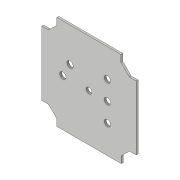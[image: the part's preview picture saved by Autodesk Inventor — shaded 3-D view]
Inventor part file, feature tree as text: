
AUTODESK INVENTOR PART (.ipt)
format: ipt  version: 2019.4 (Build 234330000, 330)  size: 149,504 bytes
history: native  units: mm
features: plane x2, extrude x2, sketch x2, hole x1, projected_geometry x1
ambient origin geometry x8: Origin, YZ Plane, XZ Plane, XY Plane, X Axis, Y Axis, Z Axis, Center Point
bodies: Body1 (feature_tree)
feature tree (8):
  plane  "Work Plane1"
  plane  "Work Plane2"
  extrude  "Extrusion1"  Depth=24.9mm
  hole  "Hole1"  [1 undecoded]
  extrude  "IM_offset"  Depth=10.0mm
  sketch  "Sketch1"  dims[d0=45.0deg d2=24.9mm]
  sketch  "Skizze6"  dims[d3=3.14mm d4=26.9mm d5=3.0mm d6=1.0mm d7=0.0mm d18=3.3mm d19=6.0mm d20=4.0mm d21=2.0mm d22=90.0deg d23=12.0mm d24=20.594885mm d25=0.2mm d26=10.0mm d27=0.0mm d28=3.0mm]
  projected_geometry  "Projizierte Kontur2"
note: 1 required parameter value undecoded (feature->parameter linkage not recoverable at this tier; creation-order binding heuristic only, values carry confidence <= 0.55)
